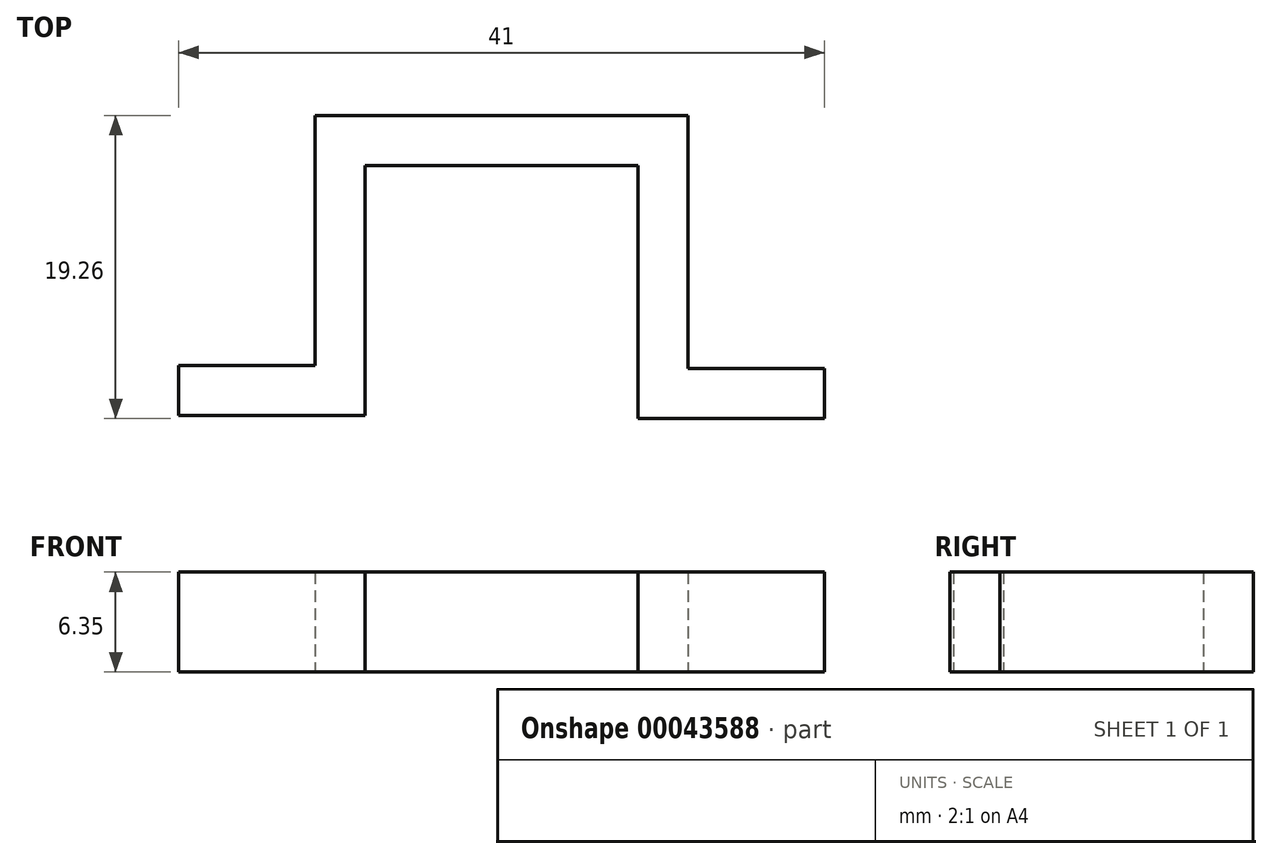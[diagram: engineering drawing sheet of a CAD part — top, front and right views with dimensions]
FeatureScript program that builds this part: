
annotation { "Feature Type Name" : "Feature", "Feature Type Description" : "" }
export const myFeature = defineFeature(function(context is Context, id is Id, definition is map)
    precondition{}
    {
        {
            var Q0;
            Q0=qCreatedBy(makeId("Top.planeOp"),FACE);
            var sketch = newSketch(context, id + "F0", { "sketchPlane" : qUnion([Q0])});
            skLineSegment(sketch, "E0", {"start": v(-11.84, 0) * mm, "end": v(-3.18, 0) * mm});
            skLineSegment(sketch, "E1", {"start": v(-3.18, 0) * mm, "end": v(-3.18, 15.88) * mm});
            skLineSegment(sketch, "E2", {"start": v(-11.84, 0) * mm, "end": v(-11.84, -3.18) * mm});
            skLineSegment(sketch, "E3", {"start": v(-11.84, -3.18) * mm, "end": v(0, -3.18) * mm});
            skLineSegment(sketch, "E4", {"start": v(0, -3.17) * mm, "end": v(0, 12.7) * mm});
            skLineSegment(sketch, "E5.MirrorCS", {"start": v(29.16, -0.2) * mm, "end": v(29.16, -3.38) * mm});
            skLineSegment(sketch, "E6.MirrorCS", {"start": v(29.16, -0.2) * mm, "end": v(20.5, -0.2) * mm});
            skLineSegment(sketch, "E7.MirrorCS", {"start": v(20.5, -0.2) * mm, "end": v(20.5, 15.88) * mm});
            skLineSegment(sketch, "E8.MirrorCS", {"start": v(29.16, -3.38) * mm, "end": v(17.32, -3.38) * mm});
            skLineSegment(sketch, "E9.MirrorCS", {"start": v(17.32, -3.38) * mm, "end": v(17.32, 12.7) * mm});
            skLineSegment(sketch, "E10", {"start": v(-3.18, 15.88) * mm, "end": v(20.5, 15.88) * mm});
            skLineSegment(sketch, "E11", {"start": v(17.32, 12.7) * mm, "end": v(0, 12.7) * mm});
            skSolve(sketch);
        }
        {
            var Q0;
            Q0 = qSketchRegion(id + "F0", true);
            extrude(context, id + "F1", {"entities" : qUnion([Q0]), "depth" : 6.35 * mm});
        }
    });
